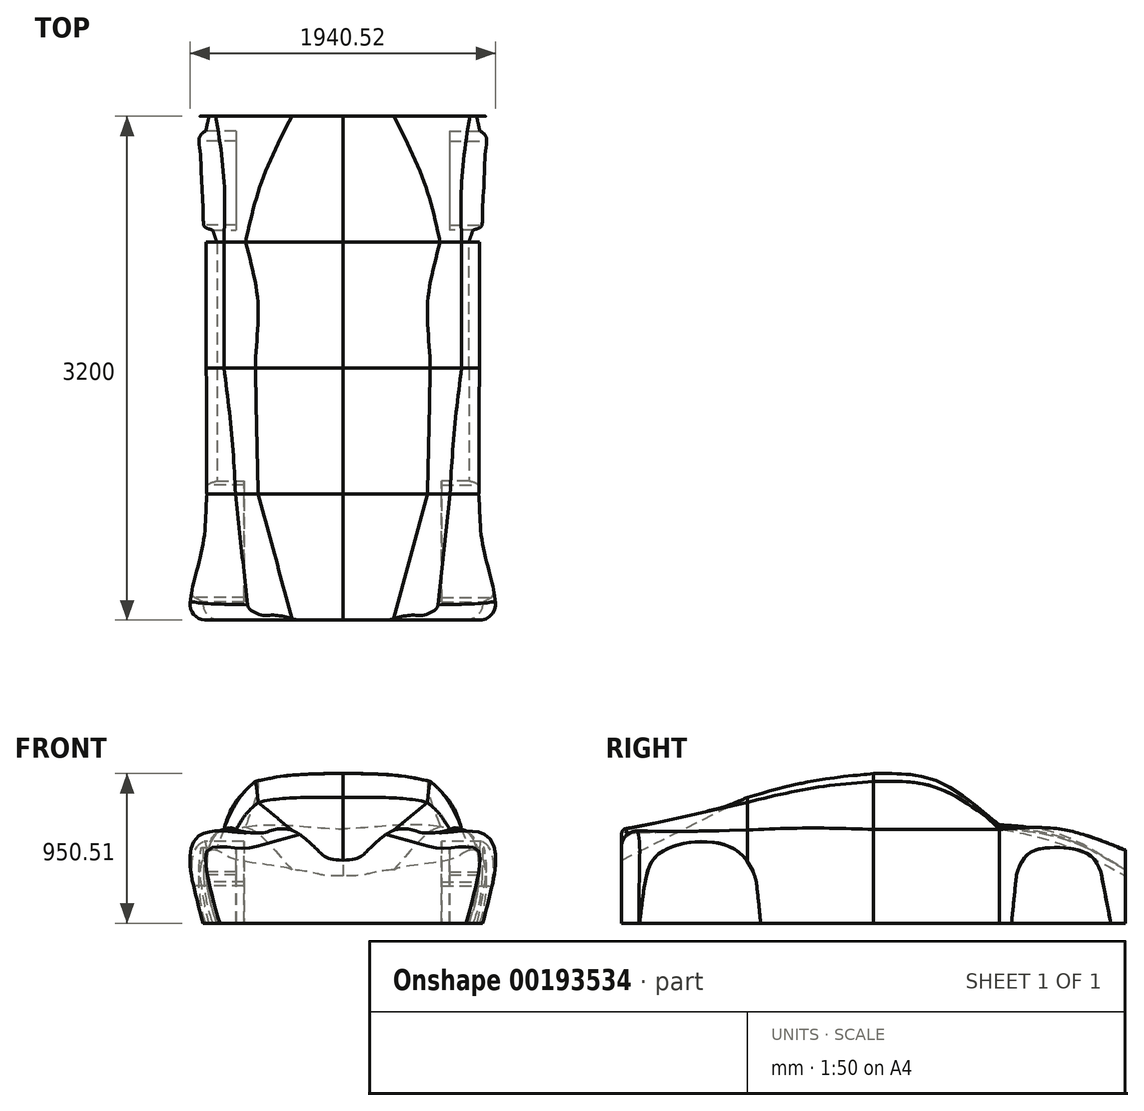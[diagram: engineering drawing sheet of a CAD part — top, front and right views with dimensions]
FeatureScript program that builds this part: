
annotation { "Feature Type Name" : "Feature", "Feature Type Description" : "" }
export const myFeature = defineFeature(function(context is Context, id is Id, definition is map)
    precondition{}
    {
        {
            var Q0;
            Q0=qCreatedBy(makeId("Front.planeOp"),FACE);
            cPlane(context, id + "F0", {"entities" : qUnion([Q0]), "cplaneType" : CPlaneType.OFFSET, "offset" : 400 * mm, "width" : 150 * mm, "height" : 150 * mm});
        }
        {
            var Q0;
            Q0=qCreatedBy(makeId("Front.planeOp"),FACE);
            cPlane(context, id + "F1", {"entities" : qUnion([Q0]), "cplaneType" : CPlaneType.OFFSET, "offset" : 400 * mm, "oppositeDirection" : true, "width" : 150 * mm, "height" : 150 * mm});
        }
        {
            var Q0;
            Q0=qCreatedBy(makeId("Front.planeOp"),FACE);
            cPlane(context, id + "F2", {"entities" : qUnion([Q0]), "cplaneType" : CPlaneType.OFFSET, "offset" : 800 * mm, "width" : 150 * mm, "height" : 150 * mm});
        }
        {
            var Q0;
            Q0=qCreatedBy(makeId("Front.planeOp"),FACE);
            cPlane(context, id + "F3", {"entities" : qUnion([Q0]), "cplaneType" : CPlaneType.OFFSET, "offset" : 800 * mm, "oppositeDirection" : true, "width" : 150 * mm, "height" : 150 * mm});
        }
        {
            var Q0;
            Q0=qCreatedBy(id+"F0.planeOp",FACE);
            var sketch = newSketch(context, id + "F4", { "sketchPlane" : qUnion([Q0])});
            skLineSegment(sketch, "E0", {"start": v(-437.64, -496.9) * mm, "end": v(362.36, -496.9) * mm});
            skFitSpline(sketch, "E1", {"points": [v(362.36, -496.9) * mm, v(411.37, -327.13) * mm, v(422.88, -64.41) * mm, v(362.36, 76.76) * mm, v(270.06, 107.64) * mm], "startDerivative": vector(197.67, 576.3) * mm, "endDerivative": vector(-315.03, 85.02) * mm});
            skFitSpline(sketch, "E2", {"points": [v(270.06, 107.64) * mm, v(225.54, 239.87) * mm, v(109.57, 359.67) * mm], "startDerivative": vector(-109.37, 364.31) * mm, "endDerivative": vector(-342.1, 275.59) * mm});
            skFitSpline(sketch, "E3", {"points": [v(109.57, 359.67) * mm, v(-93.9, 390.36) * mm, v(-437.64, 403.1) * mm], "startDerivative": vector(-435.27, 96.35) * mm, "endDerivative": vector(-663.86, -5.68) * mm});
            skLineSegment(sketch, "E4", {"start": v(-437.64, 403.1) * mm, "end": v(-437.64, -496.9) * mm});
            skSolve(sketch);
        }
        {
            var Q0;
            Q0=qCreatedBy(id+"F1.planeOp",FACE);
            var sketch = newSketch(context, id + "F5", { "sketchPlane" : qUnion([Q0])});
            skLineSegment(sketch, "E5", {"start": v(-437.64, -496.9) * mm, "end": v(362.36, -496.9) * mm});
            skFitSpline(sketch, "E6", {"points": [v(362.36, -496.9) * mm, v(411.37, -327.13) * mm, v(422.88, -64.41) * mm, v(362.36, 76.76) * mm, v(317.34, 98.7) * mm], "startDerivative": vector(197.67, 576.3) * mm, "endDerivative": vector(-315.03, 85.02) * mm});
            skFitSpline(sketch, "E7", {"points": [v(317.34, 98.7) * mm, v(233.9, 275.42) * mm, v(100.5, 364.64) * mm], "startDerivative": vector(-109.37, 364.31) * mm, "endDerivative": vector(-280.97, 134.3) * mm});
            skFitSpline(sketch, "E8", {"points": [v(100.5, 364.64) * mm, v(-101.44, 403.66) * mm, v(-437.64, 403.1) * mm], "startDerivative": vector(-435.27, 96.35) * mm, "endDerivative": vector(-663.86, -5.68) * mm});
            skLineSegment(sketch, "E9", {"start": v(-437.64, 403.1) * mm, "end": v(-437.64, -496.9) * mm});
            skSolve(sketch);
        }
        {
            var Q0;
            Q0=qCreatedBy(id+"F2.planeOp",FACE);
            var sketch = newSketch(context, id + "F6", { "sketchPlane" : qUnion([Q0])});
            skLineSegment(sketch, "E10", {"start": v(-437.64, -496.9) * mm, "end": v(362.36, -496.9) * mm});
            skFitSpline(sketch, "E11", {"points": [v(362.36, -496.9) * mm, v(411.37, -327.13) * mm, v(422.88, -64.41) * mm, v(362.36, 76.76) * mm, v(243.3, 95.74) * mm], "startDerivative": vector(197.67, 576.3) * mm, "endDerivative": vector(-315.03, 85.02) * mm});
            skFitSpline(sketch, "E12", {"points": [v(243.3, 95.74) * mm, v(189.7, 179.8) * mm, v(99.56, 271.16) * mm], "startDerivative": vector(-183.13, 286.64) * mm, "endDerivative": vector(-358.02, 310.73) * mm});
            skFitSpline(sketch, "E13", {"points": [v(99.56, 271.16) * mm, v(-96.57, 297.96) * mm, v(-437.64, 303.1) * mm], "startDerivative": vector(-435.27, 96.35) * mm, "endDerivative": vector(-663.86, -5.68) * mm});
            skLineSegment(sketch, "E14", {"start": v(-437.64, 303.1) * mm, "end": v(-437.64, -496.9) * mm});
            skSolve(sketch);
        }
        {
            var Q0;
            Q0=qCreatedBy(id+"F3.planeOp",FACE);
            var sketch = newSketch(context, id + "F7", { "sketchPlane" : qUnion([Q0])});
            skLineSegment(sketch, "E15", {"start": v(-437.64, -496.9) * mm, "end": v(362.36, -496.9) * mm});
            skFitSpline(sketch, "E16", {"points": [v(362.36, -496.9) * mm, v(411.37, -327.13) * mm, v(422.88, -64.41) * mm, v(362.36, 76.76) * mm, v(317.34, 98.7) * mm], "startDerivative": vector(197.67, 576.3) * mm, "endDerivative": vector(-315.03, 85.02) * mm});
            skFitSpline(sketch, "E17", {"points": [v(317.34, 98.7) * mm, v(232.34, 105.48) * mm, v(181.18, 115.23) * mm], "startDerivative": vector(-270.17, 31.04) * mm, "endDerivative": vector(-172.21, 37.01) * mm});
            skFitSpline(sketch, "E18", {"points": [v(181.18, 115.23) * mm, v(-108.75, 123.76) * mm, v(-437.64, 103.1) * mm], "startDerivative": vector(-435.27, 96.35) * mm, "endDerivative": vector(-663.86, -5.68) * mm});
            skLineSegment(sketch, "E19", {"start": v(-437.64, 103.1) * mm, "end": v(-437.64, -496.9) * mm});
            skSolve(sketch);
        }
        {
            var Q0;
            Q0=qCreatedBy(makeId("Front.planeOp"),FACE);
            var sketch = newSketch(context, id + "F8", { "sketchPlane" : qUnion([Q0])});
            skLineSegment(sketch, "E20", {"start": v(-437.64, -496.9) * mm, "end": v(362.36, -496.9) * mm});
            skFitSpline(sketch, "E21", {"points": [v(362.36, -496.9) * mm, v(411.37, -327.13) * mm, v(422.88, -64.41) * mm, v(362.36, 76.76) * mm, v(317.34, 98.7) * mm], "startDerivative": vector(197.67, 576.3) * mm, "endDerivative": vector(-315.03, 85.02) * mm});
            skFitSpline(sketch, "E22", {"points": [v(317.34, 98.7) * mm, v(233.9, 275.42) * mm, v(116.98, 404.65) * mm], "startDerivative": vector(-109.37, 364.31) * mm, "endDerivative": vector(-342.1, 275.59) * mm});
            skFitSpline(sketch, "E23", {"points": [v(116.98, 404.65) * mm, v(-86.1, 440.04) * mm, v(-437.64, 453.1) * mm], "startDerivative": vector(-435.27, 96.35) * mm, "endDerivative": vector(-663.86, -5.68) * mm});
            skLineSegment(sketch, "E24", {"start": v(-437.64, 453.1) * mm, "end": v(-437.64, -496.9) * mm});
            skSolve(sketch);
        }
        {
            var Q0;
            Q0=makeQuery(id+"F8.imprint","IMPRINT",FACE,{"disambiguationData":[TD([[makeQuery(id+"F8.imprint","IMPRINT",EDGE,{"derivedFrom":sQuery(id+"F8.wireOp",EDGE,"E20")}),1.0]])]});
            var Q1;
            Q1=makeQuery(id+"F4.imprint","IMPRINT",FACE,{"disambiguationData":[TD([[makeQuery(id+"F4.imprint","IMPRINT",EDGE,{"derivedFrom":sQuery(id+"F4.wireOp",EDGE,"E0")}),1.0]])]});
            var Q2;
            Q2=makeQuery(id+"F6.imprint","IMPRINT",FACE,{"disambiguationData":[TD([[makeQuery(id+"F6.imprint","IMPRINT",EDGE,{"derivedFrom":sQuery(id+"F6.wireOp",EDGE,"E10")}),1.0]])]});
            loft(context, id + "F9", {"sheetProfilesArray" : [{ "sheetProfileEntities" : qUnion([Q0]) }, { "sheetProfileEntities" : qUnion([Q1]) }, { "sheetProfileEntities" : qUnion([Q2]) }]});
        }
        {
            var Q1;
            Q1=makeQuery(id+"F9.opLoft","CAP_FACE",FACE,{"disambiguationData":[OSD([makeQuery(id+"F8.imprint","IMPRINT",FACE,{"disambiguationData":[TD([[makeQuery(id+"F8.imprint","IMPRINT",EDGE,{"derivedFrom":sQuery(id+"F8.wireOp",EDGE,"E20")}),1.0]])]})])],"isStart":true});
            var Q2;
            Q2=makeQuery(id+"F5.imprint","IMPRINT",FACE,{"disambiguationData":[TD([[makeQuery(id+"F5.imprint","IMPRINT",EDGE,{"derivedFrom":sQuery(id+"F5.wireOp",EDGE,"E5")}),1.0]])]});
            var Q3;
            Q3=makeQuery(id+"F7.imprint","IMPRINT",FACE,{"disambiguationData":[TD([[makeQuery(id+"F7.imprint","IMPRINT",EDGE,{"derivedFrom":sQuery(id+"F7.wireOp",EDGE,"E15")}),1.0]])]});
            loft(context, id + "F10", {"operationType" : NewBodyOperationType.ADD, "startCondition" : LoftEndDerivativeType.NORMAL_TO_PROFILE, "startMagnitude" : 1, "sheetProfilesArray" : [{ "sheetProfileEntities" : qUnion([Q1]) }, { "sheetProfileEntities" : qUnion([Q2]) }, { "sheetProfileEntities" : qUnion([Q3]) }]});
        }
        {
            var Q0;
            Q0=qCreatedBy(makeId("Front.planeOp"),FACE);
            cPlane(context, id + "F11", {"entities" : qUnion([Q0]), "cplaneType" : CPlaneType.OFFSET, "offset" : 1600 * mm, "width" : 150 * mm, "height" : 150 * mm});
        }
        {
            var Q0;
            Q0=qCreatedBy(id+"F11.planeOp",FACE);
            var sketch = newSketch(context, id + "F12", { "sketchPlane" : qUnion([Q0])});
            skLineSegment(sketch, "E25", {"start": v(-437.64, -496.9) * mm, "end": v(462.36, -496.9) * mm});
            skFitSpline(sketch, "E26", {"points": [v(462.36, -496.9) * mm, v(503.13, -340.23) * mm, v(548.82, -104.84) * mm, v(462.36, 76.76) * mm, v(157.92, 77.16) * mm], "startDerivative": vector(197.67, 576.3) * mm, "endDerivative": vector(-315.03, 85.02) * mm});
            skFitSpline(sketch, "E27", {"points": [v(157.92, 77.16) * mm, v(29.83, 81.91) * mm, v(-117.36, 91.62) * mm], "startDerivative": vector(-631.39, -51.17) * mm, "endDerivative": vector(-287.8, -108.16) * mm});
            skFitSpline(sketch, "E28", {"points": [v(-117.36, 91.62) * mm, v(-268.74, -23.15) * mm, v(-437.64, -96.9) * mm], "startDerivative": vector(-333.07, -142) * mm, "endDerivative": vector(-663.86, -5.68) * mm});
            skLineSegment(sketch, "E29", {"start": v(-437.64, -96.9) * mm, "end": v(-437.64, -496.9) * mm});
            skSolve(sketch);
        }
        {
            var Q1;
            Q1 = qSketchRegion(id + "F12", true);
            var Q2;
            Q2 = qSketchRegion(id + "F6", true);
            loft(context, id + "F13", {"operationType" : NewBodyOperationType.ADD, "sheetProfilesArray" : [{ "sheetProfileEntities" : qUnion([Q1]) }, { "sheetProfileEntities" : qUnion([Q2]) }]});
        }
        {
            var Q0;
            Q0=qCreatedBy(makeId("Right.planeOp"),FACE);
            cPlane(context, id + "F14", {"entities" : qUnion([Q0]), "cplaneType" : CPlaneType.OFFSET, "offset" : 800 * mm, "width" : 150 * mm, "height" : 150 * mm});
        }
        {
            var Q0;
            Q0=qCreatedBy(id+"F14.planeOp",FACE);
            var sketch = newSketch(context, id + "F15", { "sketchPlane" : qUnion([Q0])});
            skLineSegment(sketch, "E30", {"start": v(-743.36, -235.3) * mm, "end": v(-696.56, -680.73) * mm});
            skLineSegment(sketch, "E31", {"start": v(-696.56, -680.73) * mm, "end": v(-1508.45, -680.73) * mm});
            skLineSegment(sketch, "E32", {"start": v(-1508.45, -680.73) * mm, "end": v(-1455.6, -258.17) * mm});
            skFitSpline(sketch, "E33", {"points": [v(-1455.6, -258.17) * mm, v(-1367.73, -59.54) * mm, v(-939.89, 0) * mm, v(-743.36, -235.3) * mm], "startDerivative": vector(179.38, 766.9) * mm, "endDerivative": vector(215.74, -934.6) * mm});
            skSolve(sketch);
        }
        {
            var Q0;
            Q0=makeQuery(id+"F15.imprint","IMPRINT",FACE,{"disambiguationData":[TD([[makeQuery(id+"F15.imprint","IMPRINT",EDGE,{"derivedFrom":sQuery(id+"F15.wireOp",EDGE,"E30")}),-1.0]])]});
            extrude(context, id + "F16", {"entities" : qUnion([Q0]), "operationType" : NewBodyOperationType.REMOVE, "oppositeDirection" : true, "depth" : 610 * mm});
        }
        {
            var Q0;
            Q0=qCreatedBy(makeId("Front.planeOp"),FACE);
            cPlane(context, id + "F17", {"entities" : qUnion([Q0]), "cplaneType" : CPlaneType.OFFSET, "offset" : 1600 * mm, "oppositeDirection" : true, "width" : 150 * mm, "height" : 150 * mm});
        }
        {
            var Q0;
            Q0=qCreatedBy(id+"F17.planeOp",FACE);
            var sketch = newSketch(context, id + "F18", { "sketchPlane" : qUnion([Q0])});
            skLineSegment(sketch, "E34", {"start": v(-437.64, -496.9) * mm, "end": v(412.36, -496.9) * mm});
            skFitSpline(sketch, "E35", {"points": [v(412.36, -496.9) * mm, v(453.24, -312.76) * mm, v(468.47, -212.95) * mm, v(458.13, -104.07) * mm, v(368.95, -34.17) * mm], "startDerivative": vector(197.67, 576.3) * mm, "endDerivative": vector(-632.8, -161.78) * mm});
            skFitSpline(sketch, "E36", {"points": [v(368.95, -34.17) * mm, v(263.14, -86.74) * mm, v(-113.63, -157.63) * mm], "startDerivative": vector(-380.63, -87.62) * mm, "endDerivative": vector(-231.79, -133.75) * mm});
            skFitSpline(sketch, "E37", {"points": [v(-113.63, -157.63) * mm, v(-279.1, -183.63) * mm, v(-437.64, -196.9) * mm], "startDerivative": vector(-388.75, -15.86) * mm, "endDerivative": vector(-663.86, -5.68) * mm});
            skLineSegment(sketch, "E38", {"start": v(-437.64, -196.9) * mm, "end": v(-437.64, -496.9) * mm});
            skSolve(sketch);
        }
        {
            var Q0;
            Q0=qCreatedBy(id+"F17.planeOp",FACE);
            cPlane(context, id + "F19", {"entities" : qUnion([Q0]), "cplaneType" : CPlaneType.OFFSET, "offset" : 400 * mm, "width" : 150 * mm, "height" : 150 * mm});
        }
        {
            var Q0;
            Q0=qCreatedBy(id+"F19.planeOp",FACE);
            var sketch = newSketch(context, id + "F20", { "sketchPlane" : qUnion([Q0])});
            skLineSegment(sketch, "E39", {"start": v(-437.64, -496.9) * mm, "end": v(462.36, -496.9) * mm});
            skFitSpline(sketch, "E40", {"points": [v(462.36, -496.9) * mm, v(486.38, -325.83) * mm, v(475.5, -116.9) * mm, v(421.85, 53.8) * mm, v(317.34, 98.7) * mm], "startDerivative": vector(197.67, 576.3) * mm, "endDerivative": vector(-315.03, 85.02) * mm});
            skFitSpline(sketch, "E41", {"points": [v(317.34, 98.7) * mm, v(168.52, 51.04) * mm, v(72.04, 48.95) * mm], "startDerivative": vector(-360.94, 2.04) * mm, "endDerivative": vector(-390.07, 72.23) * mm});
            skFitSpline(sketch, "E42", {"points": [v(72.04, 48.95) * mm, v(-127.4, 56.45) * mm, v(-437.64, 3.1) * mm], "startDerivative": vector(-435.27, 96.35) * mm, "endDerivative": vector(-663.86, -5.68) * mm});
            skLineSegment(sketch, "E43", {"start": v(-437.64, 3.1) * mm, "end": v(-437.64, -496.9) * mm});
            skSolve(sketch);
        }
        {
            var Q1;
            Q1=makeQuery(id+"F10.opLoft","CAP_FACE",FACE,{"disambiguationData":[OSD([makeQuery(id+"F7.imprint","IMPRINT",FACE,{"disambiguationData":[TD([[makeQuery(id+"F7.imprint","IMPRINT",EDGE,{"derivedFrom":sQuery(id+"F7.wireOp",EDGE,"E15")}),1.0]])]})])],"isStart":true});
            var Q2;
            Q2=makeQuery(id+"F20.imprint","IMPRINT",FACE,{"disambiguationData":[TD([[makeQuery(id+"F20.imprint","IMPRINT",EDGE,{"derivedFrom":sQuery(id+"F20.wireOp",EDGE,"E39")}),1.0]])]});
            var Q3;
            Q3=makeQuery(id+"F18.imprint","IMPRINT",FACE,{"disambiguationData":[TD([[makeQuery(id+"F18.imprint","IMPRINT",EDGE,{"derivedFrom":sQuery(id+"F18.wireOp",EDGE,"E34")}),1.0]])]});
            loft(context, id + "F21", {"operationType" : NewBodyOperationType.ADD, "sheetProfilesArray" : [{ "sheetProfileEntities" : qUnion([Q1]) }, { "sheetProfileEntities" : qUnion([Q2]) }, { "sheetProfileEntities" : qUnion([Q3]) }]});
        }
        {
            var Q0;
            Q0=qCreatedBy(id+"F14.planeOp",FACE);
            var sketch = newSketch(context, id + "F22", { "sketchPlane" : qUnion([Q0])});
            skLineSegment(sketch, "E44", {"start": v(908.1, -190.95) * mm, "end": v(867.24, -590.52) * mm});
            skLineSegment(sketch, "E45", {"start": v(867.24, -590.52) * mm, "end": v(1525.62, -590.52) * mm});
            skLineSegment(sketch, "E46", {"start": v(1525.62, -590.52) * mm, "end": v(1443.9, -170.52) * mm});
            skFitSpline(sketch, "E47", {"points": [v(1443.9, -170.52) * mm, v(1357.62, -54.74) * mm, v(1166.92, -16.14) * mm, v(987.57, -54.74) * mm, v(908.1, -190.95) * mm], "startDerivative": vector(-221.05, 690.8) * mm, "endDerivative": vector(-187.84, -657.45) * mm});
            skSolve(sketch);
        }
        {
            var Q0;
            Q0=makeQuery(id+"F22.imprint","IMPRINT",FACE,{"disambiguationData":[TD([[makeQuery(id+"F22.imprint","IMPRINT",EDGE,{"derivedFrom":sQuery(id+"F22.wireOp",EDGE,"E44")}),1.0]])]});
            extrude(context, id + "F23", {"entities" : qUnion([Q0]), "operationType" : NewBodyOperationType.REMOVE, "oppositeDirection" : true, "depth" : 561 * mm});
        }
        {
            var Q0;
            Q0=makeQuery(id+"F13.opLoft","MID_CAP_EDGE",EDGE,{"disambiguationData":[OSD([sQuery(id+"F12.wireOp",EDGE,"E25"),sQuery(id+"F12.wireOp",EDGE,"E26"),sQuery(id+"F12.wireOp",EDGE,"E27")])],"capPos":0.0});
            fillet(context, id + "F24", {"entities" : qUnion([Q0]), "radius" : 100 * mm, "tangentPropagation" : true, "allowEdgeOverflow" : false});
        }
        {
            var Q0;
            Q0=makeQuery(id+"F9.opLoft","SWEPT_BODY",BODY,{"disambiguationData":[OSD([sQuery(id+"F4.wireOp",EDGE,"E2"),makeQuery(id+"F6.imprint","IMPRINT",FACE,{"disambiguationData":[TD([[makeQuery(id+"F6.imprint","IMPRINT",EDGE,{"derivedFrom":sQuery(id+"F6.wireOp",EDGE,"E10")}),1.0]])]}),makeQuery(id+"F8.imprint","IMPRINT",FACE,{"disambiguationData":[TD([[makeQuery(id+"F8.imprint","IMPRINT",EDGE,{"derivedFrom":sQuery(id+"F8.wireOp",EDGE,"E20")}),1.0]])]})])]});
            var Q1;
            {var subQ0=sQuery(id+"F8.wireOp",EDGE,"E24");var subQ1=sQuery(id+"F8.wireOp",EDGE,"E23");var subQ2=sQuery(id+"F8.wireOp",EDGE,"E20");Q1=makeQuery(id+"F21.boolean.opBoolean","MERGE",FACE,{"derivedFrom":[makeQuery(id+"F13.boolean.opBoolean","MERGE",FACE,{"derivedFrom":[makeQuery(id+"F10.boolean.opBoolean","MERGE",FACE,{"derivedFrom":[makeQuery(id+"F9.opLoft","SWEPT_FACE",FACE,{"disambiguationData":[OSD([sQuery(id+"F4.wireOp",EDGE,"E0"),sQuery(id+"F4.wireOp",EDGE,"E3"),sQuery(id+"F4.wireOp",EDGE,"E4"),subQ2,subQ1,subQ0])]}),makeQuery(id+"F10.opLoft","SWEPT_FACE",FACE,{"disambiguationData":[OSD([sQuery(id+"F5.wireOp",EDGE,"E5"),sQuery(id+"F5.wireOp",EDGE,"E8"),sQuery(id+"F5.wireOp",EDGE,"E9"),subQ2,subQ1,subQ0])]})]}),makeQuery(id+"F13.opLoft","SWEPT_FACE",FACE,{"disambiguationData":[OSD([sQuery(id+"F6.wireOp",EDGE,"E10"),sQuery(id+"F6.wireOp",EDGE,"E13"),sQuery(id+"F6.wireOp",EDGE,"E14"),sQuery(id+"F12.wireOp",EDGE,"E25"),sQuery(id+"F12.wireOp",EDGE,"E28"),sQuery(id+"F12.wireOp",EDGE,"E29")])]})]}),makeQuery(id+"F21.opLoft","SWEPT_FACE",FACE,{"disambiguationData":[OSD([sQuery(id+"F7.wireOp",EDGE,"E15"),sQuery(id+"F7.wireOp",EDGE,"E18"),sQuery(id+"F7.wireOp",EDGE,"E19"),sQuery(id+"F20.wireOp",EDGE,"E39"),sQuery(id+"F20.wireOp",EDGE,"E42"),sQuery(id+"F20.wireOp",EDGE,"E43")])]})]});}
            mirror(context, id + "F25", {"operationType" : NewBodyOperationType.ADD, "entities" : qUnion([Q0]), "mirrorPlane" : qUnion([Q1])});
        }
    });
